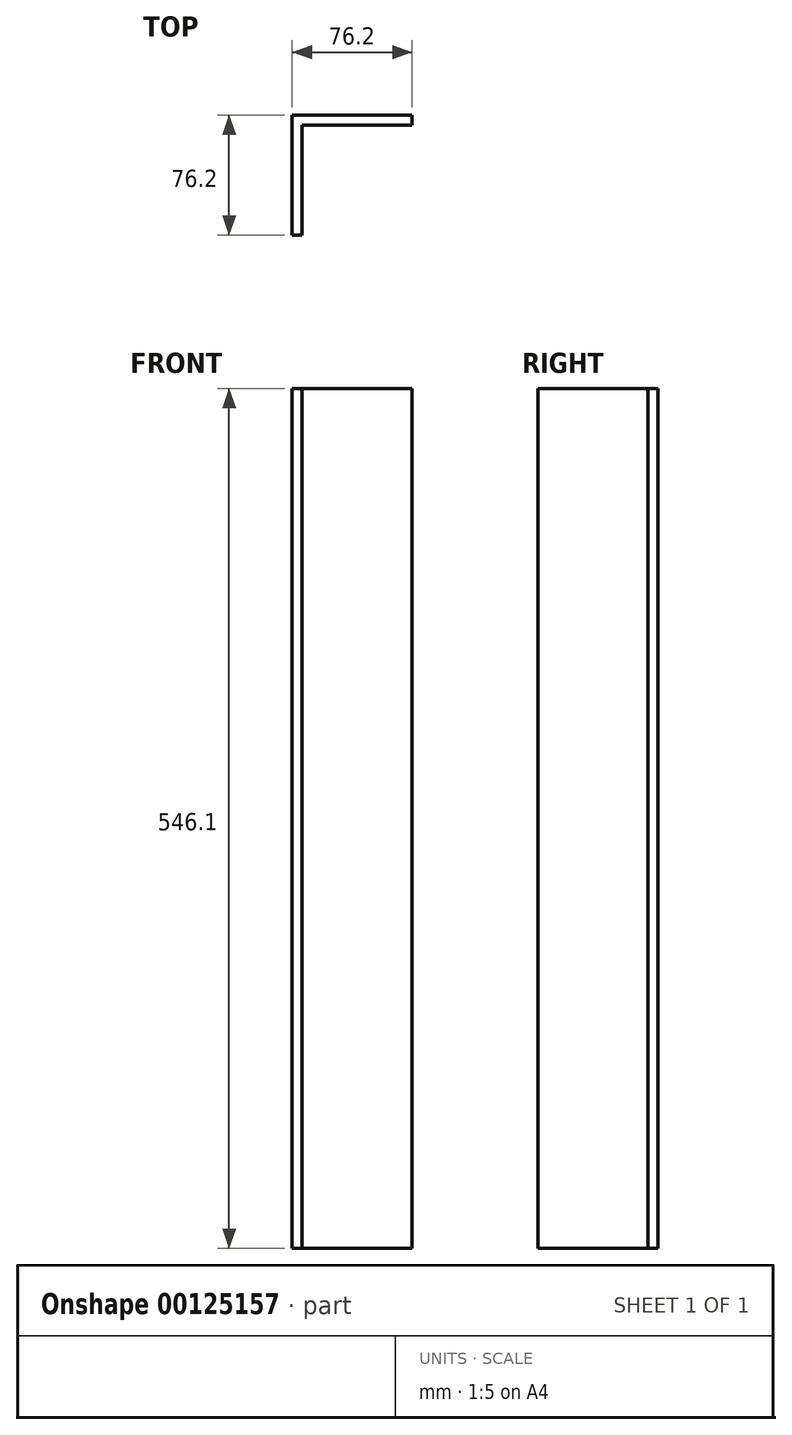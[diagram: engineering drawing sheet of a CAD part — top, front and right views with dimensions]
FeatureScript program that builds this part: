
annotation { "Feature Type Name" : "Feature", "Feature Type Description" : "" }
export const myFeature = defineFeature(function(context is Context, id is Id, definition is map)
    precondition{}
    {
        {
            var Q0;
            Q0=qCreatedBy(makeId("Top.planeOp"),FACE);
            var sketch = newSketch(context, id + "F0", { "sketchPlane" : qUnion([Q0])});
            skLineSegment(sketch, "E0", {"start": v(0, -76.2) * mm, "end": v(0, 0) * mm});
            skLineSegment(sketch, "E1", {"start": v(0, 0) * mm, "end": v(76.2, 0) * mm});
            skLineSegment(sketch, "E2.0", {"start": v(6.35, -6.35) * mm, "end": v(76.2, -6.35) * mm});
            skLineSegment(sketch, "E2.1", {"start": v(6.35, -76.2) * mm, "end": v(6.35, -6.35) * mm});
            skLineSegment(sketch, "E3", {"start": v(0, -76.2) * mm, "end": v(6.35, -76.2) * mm});
            skLineSegment(sketch, "E4", {"start": v(76.2, -6.35) * mm, "end": v(76.2, 0) * mm});
            skSolve(sketch);
        }
        {
            var Q0;
            Q0=qSketchRegion(id+"F0",true);
            extrude(context, id + "F1", {"entities" : qUnion([Q0]), "oppositeDirection" : true, "depth" : 546.1 * mm});
        }
    });
